# Revit family: Albany HS9010PFR high speed freezer door
name_source: partatom
category: Doors
revit_build: Autodesk Revit 2015 (Build: 20140606_1530(x64)
units: mm (PartAtom-declared; Revit-internal decimal feet)

## types (1)
- Albany HS9010PFR high speed freezer door
    Acoustic Signal = No
    Air permeability, EN 12426 = class 1 ,(24 m3/m2/h at 50 Pa)
/m2
/h at 50 Pa)
    Airlock = No
    Analytic Construction = <None>
    Automatic closing (Standard) = Yes
    BIMobject category = Industrial
    Brand url = http://www.assaabloyentrance.com
    Closing Speed = 1,2 m/s
    Control unit Height = 1500 mm  [stored 4.92126 ft]
    Depth = 0.00
    Design country = Sweden
    EAN code = https://EN13241-1
    Edition number = 1
    External push button box = No
    IFC Classification = Door
    Interlocking = No
    Lifetime expectations = 1.000.000 cycles
    Magnetic Loop = No
    Manufacturer country = Sweden
    Manufacturer name = ASSA ABLOY Entrance Systems
    NBS Reference Code = 59-23-38
    NBS Reference Description = High Speed Doorsets
    Nominal height = 0
    Nominal width = 0
    Opening Speed = up to 2,4 m/s 2
    Photocell Open door = No
    Product Guid = 2c0b53b3-898a-419a-a71d-716342c01539
    Product SKU = aa_a_hs9010_pfr
    Product data url = https://bimobject.com
    Product family = High speed door
    Product group = Freezer door
    Product url = http://www.crawfordsolutions.com
    Pull-rope Switch = No
    QR code = http://bimobject.com
    Radar = No
    Reduced Opening = No
    Remote Control = No
    Safety photocells 1-channel (Standard) = Yes
    Technical description = http://www.crawfordsolutions.com
    Thermal transmittance = 6,02 W/ (m2 K)
K)
    Top Cover = 500 mm  [stored 1.64042 ft]
    Traffic lights - Red & Green = No
    UNSPSC Code = 301715
    UPS battery backup = No
    Uniclass 1.4 Code = JL20
    Uniclass 1.4 Description = Doors
    Uniclass 2.0 Code = PR-59-23-38
    Uniclass 2.0 Description = High Speed Doorsets
    Warning lights - Orange = No
    Warning lights- Green = No
    Warning lights- Red = No
    Water penetration, EN 12425 = class 1 (30 N/m2)
)
    Weight Net (Kg) = 0
    Wind load resistance, EN 12424 = class 1 (300 N/m2)
)
    Wireless edge activator (Standard) = Yes
    Youtube clip = https://www.youtube.com

note: [stored X ft] marks values corroborated as IEEE doubles in the binary element streams (Revit-internal decimal feet)

## geometry (parser evidence)
native form markers: Blend x4, Sweep x5
no freeform markers — native parametric forms only
